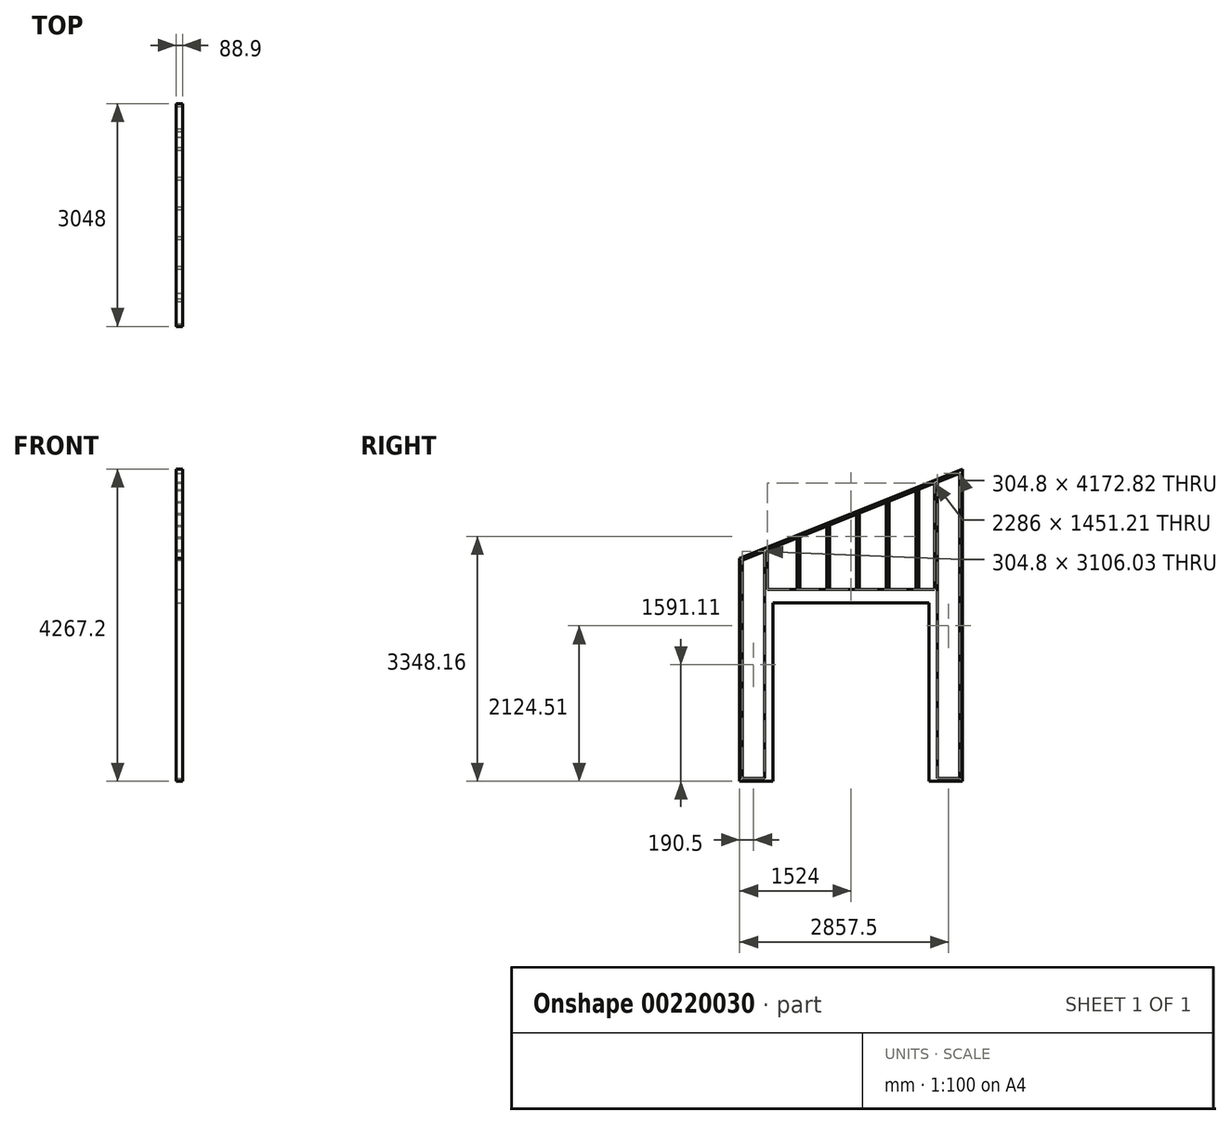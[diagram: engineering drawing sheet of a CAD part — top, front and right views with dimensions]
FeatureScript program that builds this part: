
annotation { "Feature Type Name" : "Feature", "Feature Type Description" : "" }
export const myFeature = defineFeature(function(context is Context, id is Id, definition is map)
    precondition{}
    {
        {
            var Q0;
            Q0=qCreatedBy(makeId("Right.planeOp"),FACE);
            var sketch = newSketch(context, id + "F0", { "sketchPlane" : qUnion([Q0])});
            skLineSegment(sketch, "E0", {"start": v(0, 0) * mm, "end": v(3048, 0) * mm});
            skLineSegment(sketch, "E1", {"start": v(3048, 0) * mm, "end": v(3048, 4267.2) * mm});
            skLineSegment(sketch, "E2", {"start": v(3048, 4267.2) * mm, "end": v(0, 3048) * mm});
            skLineSegment(sketch, "E3", {"start": v(0, 3048) * mm, "end": v(0, 0) * mm});
            skSolve(sketch);
        }
        {
            var Q0;
            Q0=makeQuery(id+"F0.imprint","IMPRINT",FACE,{"disambiguationData":[TD([[makeQuery(id+"F0.imprint","IMPRINT",EDGE,{"derivedFrom":sQuery(id+"F0.wireOp",EDGE,"E0")}),1.0]])]});
            extrude(context, id + "F1", {"entities" : qUnion([Q0]), "depth" : 88.9 * mm});
        }
        {
            var Q0;
            Q0=makeQuery(id+"F1.opExtrude","CAP_FACE",FACE,{"disambiguationData":[OSD([sQuery(id+"F0.wireOp",EDGE,"E0"),sQuery(id+"F0.wireOp",EDGE,"E1"),sQuery(id+"F0.wireOp",EDGE,"E2"),sQuery(id+"F0.wireOp",EDGE,"E3")])],"isStart":false});
            var sketch = newSketch(context, id + "F2", { "sketchPlane" : qUnion([Q0])});
            skLineSegment(sketch, "E4.bottom", {"start": v(457.2, 0) * mm, "end": v(2590.8, 0) * mm});
            skLineSegment(sketch, "E4.top", {"start": v(457.2, 2438.4) * mm, "end": v(2590.8, 2438.4) * mm});
            skLineSegment(sketch, "E4.left", {"start": v(457.2, 0) * mm, "end": v(457.2, 2438.4) * mm});
            skLineSegment(sketch, "E4.right", {"start": v(2590.8, 0) * mm, "end": v(2590.8, 2438.4) * mm});
            skSolve(sketch);
        }
        {
            var Q0;
            Q0=makeQuery(id+"F2.imprint","IMPRINT",FACE,{"disambiguationData":[TD([[makeQuery(id+"F2.imprint","IMPRINT",EDGE,{"derivedFrom":sQuery(id+"F2.wireOp",EDGE,"E4.bottom")}),1.0]])]});
            extrude(context, id + "F3", {"entities" : qUnion([Q0]), "operationType" : NewBodyOperationType.REMOVE, "endBound" : BoundingType.THROUGH_ALL, "oppositeDirection" : true, "depth" : 25.4 * mm});
        }
        {
            var Q0;
            Q0=makeQuery(id+"F1.opExtrude","CAP_FACE",FACE,{"disambiguationData":[OSD([sQuery(id+"F0.wireOp",EDGE,"E0"),sQuery(id+"F0.wireOp",EDGE,"E1"),sQuery(id+"F0.wireOp",EDGE,"E2"),sQuery(id+"F0.wireOp",EDGE,"E3")])],"isStart":false});
            var sketch = newSketch(context, id + "F4", { "sketchPlane" : qUnion([Q0])});
            skLineSegment(sketch, "E5.bottom", {"start": v(342.9, 2438.4) * mm, "end": v(38.1, 2438.4) * mm});
            skLineSegment(sketch, "E5.top", {"start": v(342.9, 0) * mm, "end": v(38.1, 0) * mm});
            skLineSegment(sketch, "E5.left", {"start": v(342.9, 2438.4) * mm, "end": v(342.9, 0) * mm});
            skLineSegment(sketch, "E5.right", {"start": v(38.1, 2438.4) * mm, "end": v(38.1, 0) * mm});
            skLineSegment(sketch, "E6.bottom", {"start": v(3009.9, 0) * mm, "end": v(2705.1, 0) * mm});
            skLineSegment(sketch, "E6.top", {"start": v(3009.9, 2438.4) * mm, "end": v(2705.1, 2438.4) * mm});
            skLineSegment(sketch, "E6.left", {"start": v(3009.9, 0) * mm, "end": v(3009.9, 2438.4) * mm});
            skLineSegment(sketch, "E6.right", {"start": v(2705.1, 0) * mm, "end": v(2705.1, 2438.4) * mm});
            skSolve(sketch);
        }
        {
            var Q0;
            Q0=makeQuery(id+"F4.imprint","IMPRINT",FACE,{"disambiguationData":[TD([[makeQuery(id+"F4.imprint","IMPRINT",EDGE,{"derivedFrom":sQuery(id+"F4.wireOp",EDGE,"E5.bottom")}),1.0]])]});
            var Q1;
            Q1=makeQuery(id+"F4.imprint","IMPRINT",FACE,{"disambiguationData":[TD([[makeQuery(id+"F4.imprint","IMPRINT",EDGE,{"derivedFrom":sQuery(id+"F4.wireOp",EDGE,"E6.bottom")}),1.0]])]});
            extrude(context, id + "F5", {"entities" : qUnion([Q0, Q1]), "operationType" : NewBodyOperationType.REMOVE, "endBound" : BoundingType.THROUGH_ALL, "oppositeDirection" : true, "depth" : 25.4 * mm});
        }
        {
            var Q0;
            Q0=makeQuery(id+"F1.opExtrude","CAP_FACE",FACE,{"disambiguationData":[OSD([sQuery(id+"F0.wireOp",EDGE,"E0"),sQuery(id+"F0.wireOp",EDGE,"E1"),sQuery(id+"F0.wireOp",EDGE,"E2"),sQuery(id+"F0.wireOp",EDGE,"E3")])],"isStart":false});
            var sketch = newSketch(context, id + "F6", { "sketchPlane" : qUnion([Q0])});
            skLineSegment(sketch, "E7", {"start": v(381, 2622.55) * mm, "end": v(381, 3159.37) * mm});
            skLineSegment(sketch, "E8", {"start": v(381, 3159.37) * mm, "end": v(2667, 4073.77) * mm});
            skLineSegment(sketch, "E9", {"start": v(2667, 4073.77) * mm, "end": v(2667, 2622.55) * mm});
            skLineSegment(sketch, "E10", {"start": v(2667, 2622.55) * mm, "end": v(381, 2622.55) * mm});
            skSolve(sketch);
        }
        {
            var Q0;
            Q0=makeQuery(id+"F6.imprint","IMPRINT",FACE,{"disambiguationData":[TD([[makeQuery(id+"F6.imprint","IMPRINT",EDGE,{"derivedFrom":sQuery(id+"F6.wireOp",EDGE,"E7")}),-1.0]])]});
            extrude(context, id + "F7", {"entities" : qUnion([Q0]), "operationType" : NewBodyOperationType.REMOVE, "endBound" : BoundingType.THROUGH_ALL, "oppositeDirection" : true, "depth" : 25.4 * mm});
        }
        {
            var Q0;
            Q0=makeQuery(id+"F1.opExtrude","CAP_FACE",FACE,{"disambiguationData":[OSD([sQuery(id+"F0.wireOp",EDGE,"E0"),sQuery(id+"F0.wireOp",EDGE,"E1"),sQuery(id+"F0.wireOp",EDGE,"E2"),sQuery(id+"F0.wireOp",EDGE,"E3")])],"isStart":false});
            var sketch = newSketch(context, id + "F8", { "sketchPlane" : qUnion([Q0])});
            skLineSegment(sketch, "E11", {"start": v(38.1, 2438.4) * mm, "end": v(38.1, 3022.2) * mm});
            skLineSegment(sketch, "E12", {"start": v(342.9, 2438.4) * mm, "end": v(342.9, 3144.13) * mm});
            skLineSegment(sketch, "E13", {"start": v(342.9, 3144.13) * mm, "end": v(38.1, 3022.2) * mm});
            skLineSegment(sketch, "E14", {"start": v(38.1, 2438.4) * mm, "end": v(342.9, 2438.4) * mm});
            skLineSegment(sketch, "E15", {"start": v(2705.1, 2438.4) * mm, "end": v(2705.1, 4089) * mm});
            skLineSegment(sketch, "E16", {"start": v(3009.9, 2438.4) * mm, "end": v(3009.9, 4210.93) * mm});
            skLineSegment(sketch, "E17", {"start": v(2705.1, 2438.4) * mm, "end": v(3009.9, 2438.4) * mm});
            skLineSegment(sketch, "E18", {"start": v(2705.1, 4089) * mm, "end": v(3009.9, 4210.93) * mm});
            skSolve(sketch);
        }
        {
            var Q0;
            Q0=makeQuery(id+"F8.imprint","IMPRINT",FACE,{"disambiguationData":[TD([[makeQuery(id+"F8.imprint","IMPRINT",EDGE,{"derivedFrom":sQuery(id+"F8.wireOp",EDGE,"E11")}),-1.0]])]});
            var Q1;
            Q1=makeQuery(id+"F8.imprint","IMPRINT",FACE,{"disambiguationData":[TD([[makeQuery(id+"F8.imprint","IMPRINT",EDGE,{"derivedFrom":sQuery(id+"F8.wireOp",EDGE,"E15")}),-1.0]])]});
            extrude(context, id + "F9", {"entities" : qUnion([Q0, Q1]), "operationType" : NewBodyOperationType.REMOVE, "endBound" : BoundingType.THROUGH_ALL, "oppositeDirection" : true, "depth" : 25.4 * mm});
        }
        {
            var Q0;
            Q0=makeQuery(id+"F1.opExtrude","CAP_FACE",FACE,{"disambiguationData":[OSD([sQuery(id+"F0.wireOp",EDGE,"E0"),sQuery(id+"F0.wireOp",EDGE,"E1"),sQuery(id+"F0.wireOp",EDGE,"E2"),sQuery(id+"F0.wireOp",EDGE,"E3")])],"isStart":false});
            var sketch = newSketch(context, id + "F10", { "sketchPlane" : qUnion([Q0])});
            skLineSegment(sketch, "E19", {"start": v(787.4, 3321.93) * mm, "end": v(787.4, 2622.55) * mm});
            skLineSegment(sketch, "E20", {"start": v(787.4, 2622.55) * mm, "end": v(825.5, 2622.55) * mm});
            skLineSegment(sketch, "E21", {"start": v(825.5, 2622.55) * mm, "end": v(825.5, 3337.17) * mm});
            skLineSegment(sketch, "E22", {"start": v(825.5, 3337.17) * mm, "end": v(787.4, 3321.93) * mm});
            skLineSegment(sketch, "E23", {"start": v(1193.8, 3484.49) * mm, "end": v(1193.8, 2622.55) * mm});
            skLineSegment(sketch, "E24", {"start": v(1193.8, 2622.55) * mm, "end": v(1231.9, 2622.55) * mm});
            skLineSegment(sketch, "E25", {"start": v(1231.9, 2622.55) * mm, "end": v(1231.9, 3499.73) * mm});
            skLineSegment(sketch, "E26", {"start": v(1231.9, 3499.73) * mm, "end": v(1193.8, 3484.49) * mm});
            skLineSegment(sketch, "E27", {"start": v(1600.2, 3647.05) * mm, "end": v(1600.2, 2622.55) * mm});
            skLineSegment(sketch, "E28", {"start": v(1600.2, 2622.55) * mm, "end": v(1638.3, 2622.55) * mm});
            skLineSegment(sketch, "E29", {"start": v(1638.3, 2622.55) * mm, "end": v(1638.3, 3662.29) * mm});
            skLineSegment(sketch, "E30", {"start": v(1638.3, 3662.29) * mm, "end": v(1600.2, 3647.05) * mm});
            skLineSegment(sketch, "E31", {"start": v(2006.6, 3809.6) * mm, "end": v(2006.6, 2622.55) * mm});
            skLineSegment(sketch, "E32", {"start": v(2006.6, 2622.55) * mm, "end": v(2044.7, 2622.55) * mm});
            skLineSegment(sketch, "E33", {"start": v(2044.7, 2622.55) * mm, "end": v(2044.7, 3824.85) * mm});
            skLineSegment(sketch, "E34", {"start": v(2044.7, 3824.85) * mm, "end": v(2006.6, 3809.6) * mm});
            skLineSegment(sketch, "E35", {"start": v(2413, 3972.17) * mm, "end": v(2413, 2622.55) * mm});
            skLineSegment(sketch, "E36", {"start": v(2413, 2622.55) * mm, "end": v(2451.1, 2622.55) * mm});
            skLineSegment(sketch, "E37", {"start": v(2451.1, 2622.55) * mm, "end": v(2451.1, 3987.4) * mm});
            skLineSegment(sketch, "E38", {"start": v(2451.1, 3987.4) * mm, "end": v(2413, 3972.17) * mm});
            skSolve(sketch);
        }
        {
            var Q0;
            Q0=makeQuery(id+"F10.imprint","IMPRINT",FACE,{"disambiguationData":[TD([[makeQuery(id+"F10.imprint","IMPRINT",EDGE,{"derivedFrom":sQuery(id+"F10.wireOp",EDGE,"E19")}),1.0]])]});
            var Q1;
            Q1=makeQuery(id+"F10.imprint","IMPRINT",FACE,{"disambiguationData":[TD([[makeQuery(id+"F10.imprint","IMPRINT",EDGE,{"derivedFrom":sQuery(id+"F10.wireOp",EDGE,"E23")}),1.0]])]});
            var Q2;
            Q2=makeQuery(id+"F10.imprint","IMPRINT",FACE,{"disambiguationData":[TD([[makeQuery(id+"F10.imprint","IMPRINT",EDGE,{"derivedFrom":sQuery(id+"F10.wireOp",EDGE,"E27")}),1.0]])]});
            var Q3;
            Q3=makeQuery(id+"F10.imprint","IMPRINT",FACE,{"disambiguationData":[TD([[makeQuery(id+"F10.imprint","IMPRINT",EDGE,{"derivedFrom":sQuery(id+"F10.wireOp",EDGE,"E31")}),1.0]])]});
            var Q4;
            Q4=makeQuery(id+"F10.imprint","IMPRINT",FACE,{"disambiguationData":[TD([[makeQuery(id+"F10.imprint","IMPRINT",EDGE,{"derivedFrom":sQuery(id+"F10.wireOp",EDGE,"E35")}),1.0]])]});
            extrude(context, id + "F11", {"entities" : qUnion([Q0, Q1, Q2, Q3, Q4]), "oppositeDirection" : true, "depth" : 88.9 * mm});
        }
        {
            var Q0;
            Q0=makeQuery(id+"F1.opExtrude","CAP_FACE",FACE,{"disambiguationData":[OSD([sQuery(id+"F0.wireOp",EDGE,"E0"),sQuery(id+"F0.wireOp",EDGE,"E1"),sQuery(id+"F0.wireOp",EDGE,"E2"),sQuery(id+"F0.wireOp",EDGE,"E3")])],"isStart":false});
            var sketch = newSketch(context, id + "F12", { "sketchPlane" : qUnion([Q0])});
            skLineSegment(sketch, "E39.bottom", {"start": v(38.1, 0) * mm, "end": v(342.9, 0) * mm});
            skLineSegment(sketch, "E39.top", {"start": v(38.1, 38.1) * mm, "end": v(342.9, 38.1) * mm});
            skLineSegment(sketch, "E39.left", {"start": v(38.1, 0) * mm, "end": v(38.1, 38.1) * mm});
            skLineSegment(sketch, "E39.right", {"start": v(342.9, 0) * mm, "end": v(342.9, 38.1) * mm});
            skLineSegment(sketch, "E40.bottom", {"start": v(2705.1, 0) * mm, "end": v(3009.9, 0) * mm});
            skLineSegment(sketch, "E40.top", {"start": v(2705.1, 38.1) * mm, "end": v(3009.9, 38.1) * mm});
            skLineSegment(sketch, "E40.left", {"start": v(2705.1, 0) * mm, "end": v(2705.1, 38.1) * mm});
            skLineSegment(sketch, "E40.right", {"start": v(3009.9, 0) * mm, "end": v(3009.9, 38.1) * mm});
            skSolve(sketch);
        }
        {
            var Q0;
            Q0=makeQuery(id+"F12.imprint","IMPRINT",FACE,{"disambiguationData":[TD([[makeQuery(id+"F12.imprint","IMPRINT",EDGE,{"derivedFrom":sQuery(id+"F12.wireOp",EDGE,"E39.bottom")}),1.0]])]});
            var Q1;
            Q1=makeQuery(id+"F12.imprint","IMPRINT",FACE,{"disambiguationData":[TD([[makeQuery(id+"F12.imprint","IMPRINT",EDGE,{"derivedFrom":sQuery(id+"F12.wireOp",EDGE,"E40.bottom")}),1.0]])]});
            extrude(context, id + "F13", {"entities" : qUnion([Q0, Q1]), "operationType" : NewBodyOperationType.ADD, "oppositeDirection" : true, "depth" : 88.9 * mm});
        }
    });
